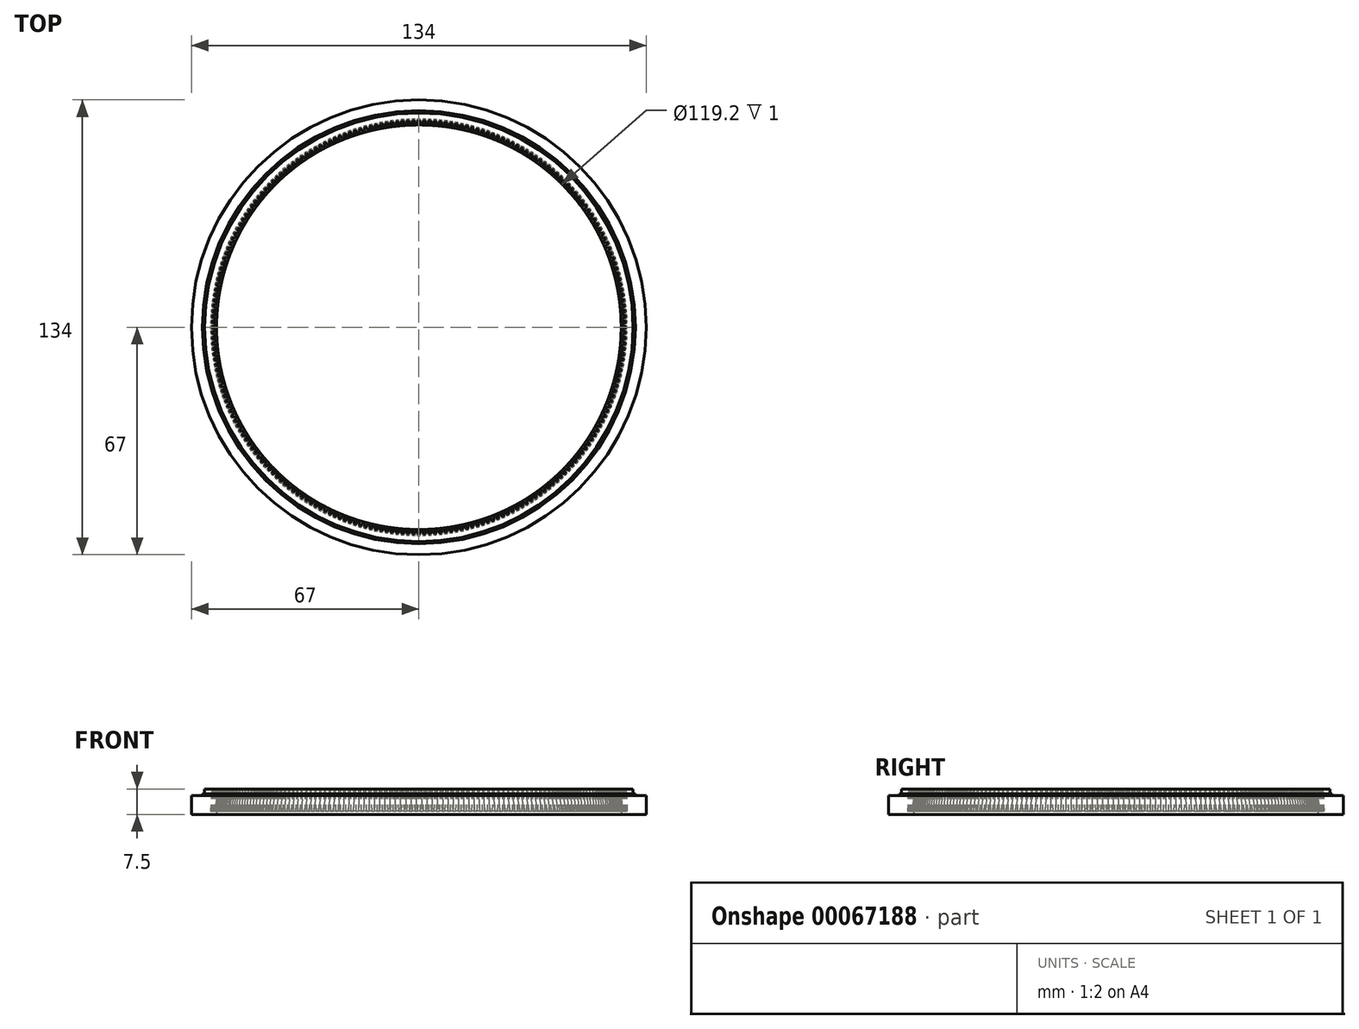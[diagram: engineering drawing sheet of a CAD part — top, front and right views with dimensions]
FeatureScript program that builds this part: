
annotation { "Feature Type Name" : "Feature", "Feature Type Description" : "" }
export const myFeature = defineFeature(function(context is Context, id is Id, definition is map)
    precondition{}
    {
        {
            var Q0;
            Q0=qCreatedBy(makeId("Top.planeOp"),FACE);
            var sketch = newSketch(context, id + "F0", { "sketchPlane" : qUnion([Q0])});
            skCircle(sketch, "E0", {"center": v(0, 0) * mm, "radius": 59.6 * mm});
            skCircle(sketch, "E1", {"center": v(0, 0) * mm, "radius": 67 * mm});
            skSolve(sketch);
        }
        {
            var Q0;
            Q0=makeQuery(id+"F0.imprint","IMPRINT",FACE,{"disambiguationData":[TD([[makeQuery(id+"F0.imprint","IMPRINT",EDGE,{"derivedFrom":sQuery(id+"F0.wireOp",EDGE,"E0")}),-1.0]])]});
            extrude(context, id + "F1", {"entities" : qUnion([Q0]), "endBound" : BoundingType.SYMMETRIC, "depth" : 7.5 * mm});
        }
        {
            var Q0;
            Q0=makeQuery(id+"F1.opExtrude","CAP_FACE",FACE,{"disambiguationData":[OSD([sQuery(id+"F0.wireOp",EDGE,"E0"),sQuery(id+"F0.wireOp",EDGE,"E1")])],"isStart":false});
            var sketch = newSketch(context, id + "F2", { "sketchPlane" : qUnion([Q0])});
            skCircle(sketch, "E2", {"center": v(0, 0) * mm, "radius": 63.12 * mm});
            skCircle(sketch, "E3", {"center": v(0, 0) * mm, "radius": 63.88 * mm});
            skSolve(sketch);
        }
        {
            var Q0;
            Q0=makeQuery(id+"F2.imprint","IMPRINT",FACE,{"disambiguationData":[TD([[makeQuery(id+"F2.imprint","IMPRINT",EDGE,{"derivedFrom":sQuery(id+"F2.wireOp",EDGE,"E2")}),-1.0]])]});
            extrude(context, id + "F3", {"entities" : qUnion([Q0]), "operationType" : NewBodyOperationType.REMOVE, "oppositeDirection" : true, "depth" : 1.5 * mm});
        }
        {
            var Q0;
            {var subQ0=sQuery(id+"F0.wireOp",EDGE,"E1");Q0=makeQuery(id+"F3.boolean.opBoolean","SPLIT",FACE,{"disambiguationData":[TD([makeQuery(id+"F1.opExtrude","SWEPT_FACE",FACE,{"disambiguationData":[OSD([subQ0])]})])],"derivedFrom":makeQuery(id+"F1.opExtrude","CAP_FACE",FACE,{"disambiguationData":[OSD([sQuery(id+"F0.wireOp",EDGE,"E0"),subQ0])],"isStart":false})});}
            extrude(context, id + "F4", {"entities" : qUnion([Q0]), "operationType" : NewBodyOperationType.REMOVE, "oppositeDirection" : true, "depth" : 2 * mm, "hasDraft" : true, "draftAngle" : 3 * degree});
        }
        {
            var Q0;
            Q0=qCreatedBy(makeId("Top.planeOp"),FACE);
            var sketch = newSketch(context, id + "F5", { "sketchPlane" : qUnion([Q0])});
            skCircle(sketch, "E4", {"center": v(0, 0) * mm, "radius": 61 * mm, "construction": true});
            skLineSegment(sketch, "E5", {"start": v(0, 0) * mm, "end": v(61, 0) * mm, "construction": true});
            skLineSegment(sketch, "E6", {"start": v(61, -0.15) * mm, "end": v(61, 0.15) * mm});
            skLineSegment(sketch, "E7", {"start": v(59.4, -0.67) * mm, "end": v(59.4, 0.67) * mm});
            skLineSegment(sketch, "E8", {"start": v(61, 0) * mm, "end": v(59.4, 0) * mm, "construction": true});
            skLineSegment(sketch, "E9", {"start": v(59.4, 0.67) * mm, "end": v(61, 0.15) * mm});
            skLineSegment(sketch, "E10", {"start": v(61, -0.15) * mm, "end": v(59.4, -0.67) * mm});
            skSolve(sketch);
        }
        {
            var Q0;
            {var subQ0=sQuery(id+"F0.wireOp",EDGE,"E0");Q0=makeQuery(id+"F3.boolean.opBoolean","SPLIT",FACE,{"disambiguationData":[TD([makeQuery(id+"F1.opExtrude","SWEPT_FACE",FACE,{"disambiguationData":[OSD([subQ0])]})])],"derivedFrom":makeQuery(id+"F1.opExtrude","CAP_FACE",FACE,{"disambiguationData":[OSD([subQ0,sQuery(id+"F0.wireOp",EDGE,"E1")])],"isStart":false})});}
            var sketch = newSketch(context, id + "F6", { "sketchPlane" : qUnion([Q0])});
            skLineSegment(sketch, "E11.0", {"start": v(59.4, 0.67) * mm, "end": v(61, 0.15) * mm});
            skLineSegment(sketch, "E11.1", {"start": v(59.4, -0.67) * mm, "end": v(59.4, 0.67) * mm});
            skLineSegment(sketch, "E11.2", {"start": v(61, -0.15) * mm, "end": v(59.4, -0.67) * mm});
            skLineSegment(sketch, "E11.3", {"start": v(61, -0.15) * mm, "end": v(61, 0.15) * mm});
            skCircle(sketch, "E12.0", {"center": v(0, 0) * mm, "radius": 61 * mm, "construction": true});
            skSolve(sketch);
        }
        {
            var Q0;
            Q0 = qSketchRegion(id + "F6", true);
            extrude(context, id + "F7", {"entities" : qUnion([Q0]), "operationType" : NewBodyOperationType.REMOVE, "oppositeDirection" : true, "depth" : 6.5 * mm, "hasDraft" : true, "draftAngle" : 3 * degree});
        }
        {
            var Q0;
            Q0=makeQuery(id+"F7.boolean.opBoolean","COPY",FACE,{"derivedFrom":makeQuery(id+"F7.opExtrude","SWEPT_FACE",FACE,{"disambiguationData":[OSD([sQuery(id+"F6.wireOp",EDGE,"E11.0")])]})});
            var Q1;
            Q1=makeQuery(id+"F7.boolean.opBoolean","COPY",FACE,{"derivedFrom":makeQuery(id+"F7.opExtrude","SWEPT_FACE",FACE,{"disambiguationData":[OSD([sQuery(id+"F6.wireOp",EDGE,"E11.3")])]})});
            var Q2;
            Q2=makeQuery(id+"F7.boolean.opBoolean","COPY",FACE,{"derivedFrom":makeQuery(id+"F7.opExtrude","SWEPT_FACE",FACE,{"disambiguationData":[OSD([sQuery(id+"F6.wireOp",EDGE,"E11.2")])]})});
            var Q3;
            Q3=makeQuery(id+"F7.boolean.opBoolean","COPY",FACE,{"derivedFrom":makeQuery(id+"F7.opExtrude","CAP_FACE",FACE,{"disambiguationData":[OSD([sQuery(id+"F6.wireOp",EDGE,"E11.0"),sQuery(id+"F6.wireOp",EDGE,"E11.1"),sQuery(id+"F6.wireOp",EDGE,"E11.2"),sQuery(id+"F6.wireOp",EDGE,"E11.3")])],"isStart":false})});
            var Q4;
            Q4=sQuery(id+"F5.wireOp",EDGE,"E4");
            circularPattern(context, id + "F8", {"faces" : qUnion([Q0, Q1, Q2, Q3]), "axis" : qUnion([Q4]), "angle" : 360 * degree, "instanceCount" : 240, "oppositeDirection" : true, "equalSpace" : true, "patternType" : PatternType.FACE});
        }
    });
